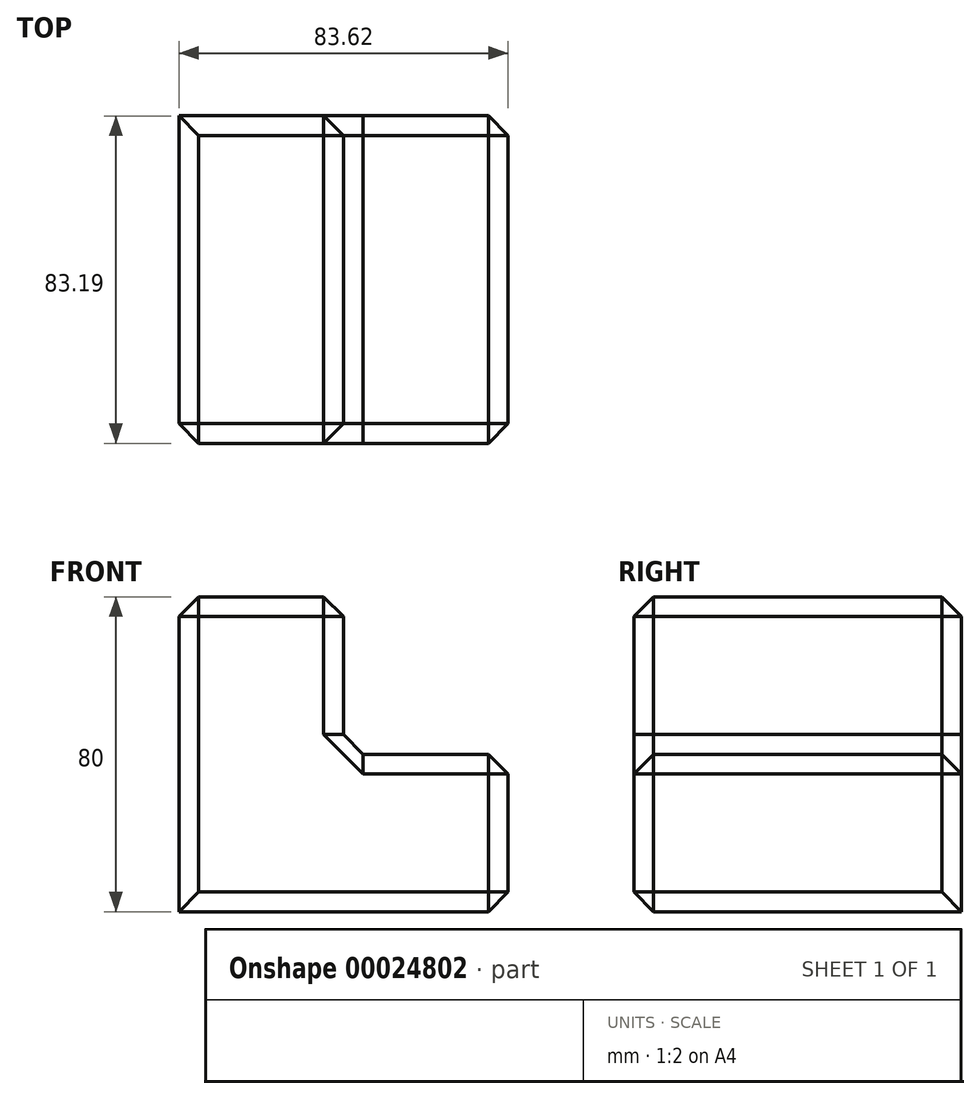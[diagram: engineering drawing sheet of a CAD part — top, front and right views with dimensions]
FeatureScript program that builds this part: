
annotation { "Feature Type Name" : "Feature", "Feature Type Description" : "" }
export const myFeature = defineFeature(function(context is Context, id is Id, definition is map)
    precondition{}
    {
        {
            var Q0;
            Q0=qCreatedBy(makeId("Top.planeOp"),FACE);
            var sketch = newSketch(context, id + "F0", { "sketchPlane" : qUnion([Q0])});
            skLineSegment(sketch, "E0.bottom", {"start": v(-59.13, -45.93) * mm, "end": v(24.5, -45.93) * mm});
            skLineSegment(sketch, "E0.top", {"start": v(-59.13, 37.26) * mm, "end": v(24.5, 37.26) * mm});
            skLineSegment(sketch, "E0.left", {"start": v(-59.13, -45.93) * mm, "end": v(-59.13, 37.26) * mm});
            skLineSegment(sketch, "E0.right", {"start": v(24.5, -45.93) * mm, "end": v(24.5, 37.26) * mm});
            skSolve(sketch);
        }
        {
            var Q0;
            Q0=makeQuery(id+"F0.imprint","IMPRINT",FACE,{"disambiguationData":[TD([[makeQuery(id+"F0.imprint","IMPRINT",EDGE,{"derivedFrom":sQuery(id+"F0.wireOp",EDGE,"E0.bottom")}),1.0]])]});
            extrude(context, id + "F1", {"entities" : qUnion([Q0]), "depth" : 40 * mm});
        }
        {
            var Q0;
            Q0=makeQuery(id+"F1.opExtrude","CAP_FACE",FACE,{"disambiguationData":[OSD([sQuery(id+"F0.wireOp",EDGE,"E0.bottom"),sQuery(id+"F0.wireOp",EDGE,"E0.top"),sQuery(id+"F0.wireOp",EDGE,"E0.left"),sQuery(id+"F0.wireOp",EDGE,"E0.right")])],"isStart":false});
            var sketch = newSketch(context, id + "F2", { "sketchPlane" : qUnion([Q0])});
            skLineSegment(sketch, "E1", {"start": v(-17.32, 37.26) * mm, "end": v(-17.32, -45.93) * mm});
            skSolve(sketch);
        }
        {
            var Q0;
            {var subQ1=sQuery(id+"F2.wireOp",EDGE,"E1");Q0=makeQuery(id+"F2.imprint","IMPRINT",FACE,{"disambiguationData":[TD([[makeQuery(id+"F2.imprint","IMPRINT",EDGE,{"derivedFrom":subQ1}),-1.0]])]});}
            extrude(context, id + "F3", {"entities" : qUnion([Q0]), "operationType" : NewBodyOperationType.ADD, "depth" : 40 * mm});
        }
        {
            var Q0;
            Q0=makeQuery(id+"F3.opExtrude","CAP_FACE",FACE,{"disambiguationData":[OSD([sQuery(id+"F0.wireOp",EDGE,"E0.bottom"),sQuery(id+"F0.wireOp",EDGE,"E0.top"),sQuery(id+"F0.wireOp",EDGE,"E0.left"),sQuery(id+"F2.wireOp",EDGE,"E1")])],"isStart":false});
            var Q1;
            Q1=makeQuery(id+"F3.opExtrude","SWEPT_FACE",FACE,{"disambiguationData":[OSD([sQuery(id+"F2.wireOp",EDGE,"E1")])]});
            var Q2;
            Q2=makeQuery(id+"F1.opExtrude","CAP_FACE",FACE,{"disambiguationData":[OSD([sQuery(id+"F0.wireOp",EDGE,"E0.bottom"),sQuery(id+"F0.wireOp",EDGE,"E0.top"),sQuery(id+"F0.wireOp",EDGE,"E0.left"),sQuery(id+"F0.wireOp",EDGE,"E0.right")])],"isStart":false});
            var Q3;
            Q3=makeQuery(id+"F1.opExtrude","SWEPT_FACE",FACE,{"disambiguationData":[OSD([sQuery(id+"F0.wireOp",EDGE,"E0.right")])]});
            var Q4;
            {var subQ0=sQuery(id+"F0.wireOp",EDGE,"E0.bottom");Q4=makeQuery(id+"F3.boolean.opBoolean","MERGE",FACE,{"derivedFrom":[makeQuery(id+"F1.opExtrude","SWEPT_FACE",FACE,{"disambiguationData":[OSD([subQ0])]}),makeQuery(id+"F3.opExtrude","SWEPT_FACE",FACE,{"disambiguationData":[OSD([subQ0])]})]});}
            chamfer(context, id + "F4", {"entities" : qUnion([Q0, Q1, Q2, Q3, Q4]), "width" : 5 * mm, "tangentPropagation" : true});
        }
    });
